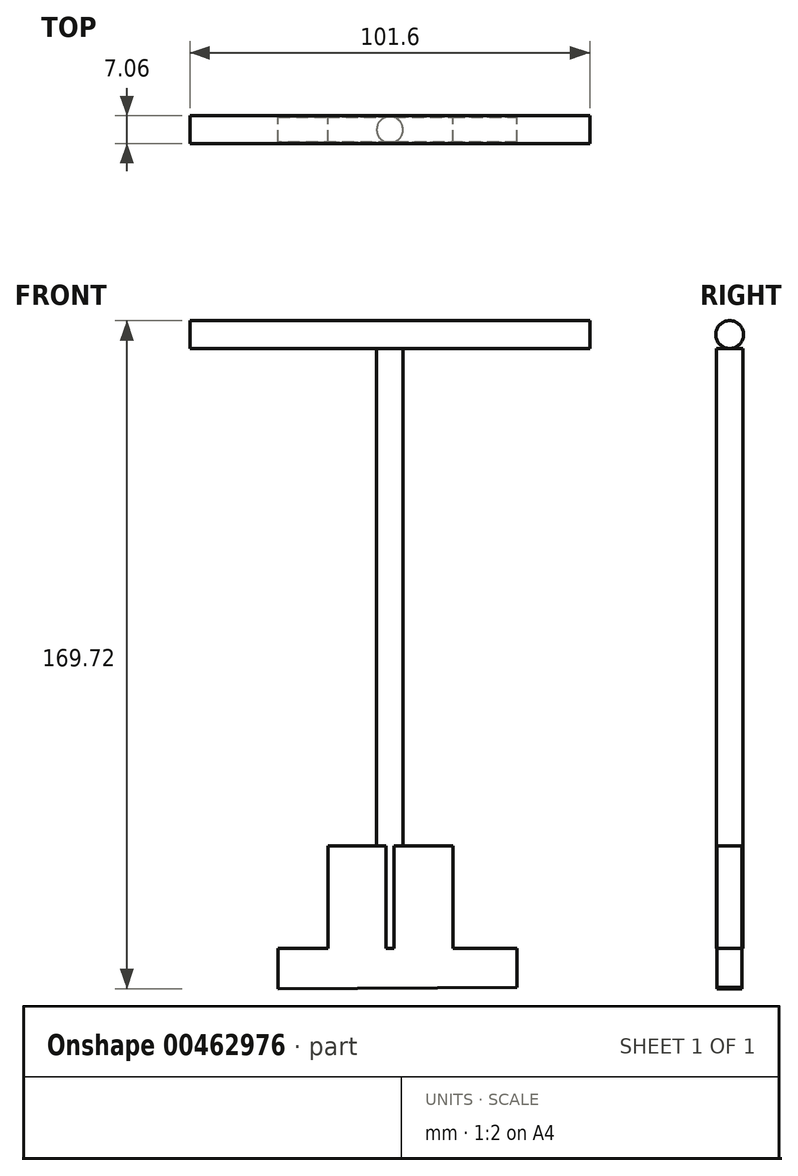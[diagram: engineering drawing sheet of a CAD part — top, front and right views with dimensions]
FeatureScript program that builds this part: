
annotation { "Feature Type Name" : "Feature", "Feature Type Description" : "" }
export const myFeature = defineFeature(function(context is Context, id is Id, definition is map)
    precondition{}
    {
        {
            var Q0;
            Q0=qCreatedBy(makeId("Front.planeOp"),FACE);
            var sketch = newSketch(context, id + "F0", { "sketchPlane" : qUnion([Q0])});
            skLineSegment(sketch, "E0", {"start": v(-28.37, -10.25) * mm, "end": v(-28.37, 0) * mm});
            skLineSegment(sketch, "E1", {"start": v(-28.37, 0) * mm, "end": v(-15.73, 0) * mm});
            skLineSegment(sketch, "E2", {"start": v(-15.73, 0) * mm, "end": v(-15.73, 26.05) * mm});
            skLineSegment(sketch, "E3", {"start": v(-15.73, 26.05) * mm, "end": v(16.1, 26.05) * mm});
            skLineSegment(sketch, "E4", {"start": v(16.1, 26.05) * mm, "end": v(16.1, 0) * mm});
            skLineSegment(sketch, "E5", {"start": v(16.1, 0) * mm, "end": v(32.3, 0) * mm});
            skLineSegment(sketch, "E6", {"start": v(32.3, 0) * mm, "end": v(32.3, -9.88) * mm});
            skLineSegment(sketch, "E7", {"start": v(32.3, -9.88) * mm, "end": v(-28.37, -10.25) * mm});
            skSolve(sketch);
        }
        {
            var Q0;
            Q0=makeQuery(id+"F0.imprint","IMPRINT",FACE,{"disambiguationData":[TD([[makeQuery(id+"F0.imprint","IMPRINT",EDGE,{"derivedFrom":sQuery(id+"F0.wireOp",EDGE,"E0")}),-1.0]])]});
            extrude(context, id + "F1", {"entities" : qUnion([Q0]), "endBound" : BoundingType.SYMMETRIC, "depth" : 6.35 * mm});
        }
        {
            var Q0;
            Q0=qCreatedBy(makeId("Top.planeOp"),FACE);
            var sketch = newSketch(context, id + "F2", { "sketchPlane" : qUnion([Q0])});
            skCircle(sketch, "E8", {"center": v(0, 0) * mm, "radius": 3.33 * mm});
            skSolve(sketch);
        }
        {
            var Q0;
            Q0=makeQuery(id+"F2.imprint","IMPRINT",FACE,{"disambiguationData":[TD([[makeQuery(id+"F2.imprint","IMPRINT",EDGE,{"derivedFrom":sQuery(id+"F2.wireOp",EDGE,"E8")}),1.0]])]});
            extrude(context, id + "F3", {"entities" : qUnion([Q0]), "operationType" : NewBodyOperationType.ADD, "depth" : 152.4 * mm});
        }
        {
            var Q0;
            Q0=qCreatedBy(makeId("Right.planeOp"),FACE);
            var sketch = newSketch(context, id + "F4", { "sketchPlane" : qUnion([Q0])});
            skCircle(sketch, "E9", {"center": v(0, 155.94) * mm, "radius": 3.53 * mm});
            skSolve(sketch);
        }
        {
            var Q0;
            Q0=makeQuery(id+"F4.imprint","IMPRINT",FACE,{"disambiguationData":[TD([[makeQuery(id+"F4.imprint","IMPRINT",EDGE,{"derivedFrom":sQuery(id+"F4.wireOp",EDGE,"E9")}),1.0]])]});
            extrude(context, id + "F5", {"entities" : qUnion([Q0]), "endBound" : BoundingType.SYMMETRIC, "depth" : 101.6 * mm});
        }
    });
